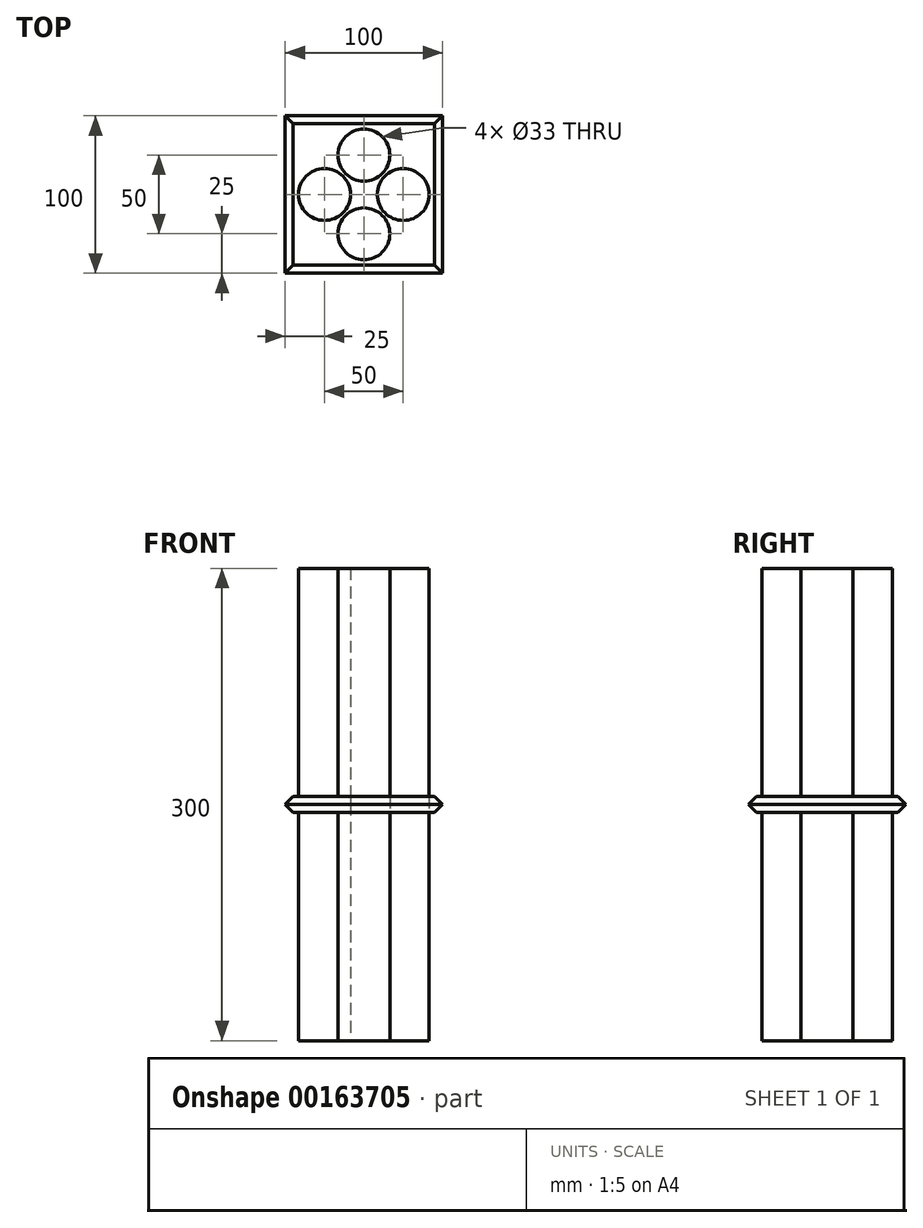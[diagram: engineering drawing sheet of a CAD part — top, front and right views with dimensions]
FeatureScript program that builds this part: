
annotation { "Feature Type Name" : "Feature", "Feature Type Description" : "" }
export const myFeature = defineFeature(function(context is Context, id is Id, definition is map)
    precondition{}
    {
        {
            var Q0;
            Q0=qCreatedBy(makeId("Top.planeOp"),FACE);
            var sketch = newSketch(context, id + "F0", { "sketchPlane" : qUnion([Q0])});
            skLineSegment(sketch, "E0.bottom", {"start": v(50, 50) * mm, "end": v(-50, 50) * mm});
            skLineSegment(sketch, "E0.top", {"start": v(50, -50) * mm, "end": v(-50, -50) * mm});
            skLineSegment(sketch, "E0.left", {"start": v(50, 50) * mm, "end": v(50, -50) * mm});
            skLineSegment(sketch, "E0.right", {"start": v(-50, 50) * mm, "end": v(-50, -50) * mm});
            skPoint(sketch, "E0.middle", {"position": v(0, 0) * mm});
            skCircle(sketch, "E1", {"center": v(25, 0) * mm, "radius": 16.5 * mm});
            skCircle(sketch, "E2", {"center": v(-25, 0) * mm, "radius": 16.5 * mm});
            skCircle(sketch, "E3", {"center": v(0, 25) * mm, "radius": 16.5 * mm});
            skCircle(sketch, "E4", {"center": v(0, -25) * mm, "radius": 16.5 * mm});
            skLineSegment(sketch, "E5", {"start": v(-25, 0) * mm, "end": v(-25, -33.27) * mm});
            skLineSegment(sketch, "E6", {"start": v(0, -25) * mm, "end": v(35.94, -25) * mm});
            skLineSegment(sketch, "E7", {"start": v(25, 0) * mm, "end": v(25, 37.48) * mm});
            skLineSegment(sketch, "E8", {"start": v(0, 25) * mm, "end": v(-38.74, 25) * mm});
            skSolve(sketch);
        }
        {
            var Q0;
            Q0=makeQuery(id+"F0.imprint","IMPRINT",FACE,{"disambiguationData":[TD([[makeQuery(id+"F0.imprint","IMPRINT",EDGE,{"derivedFrom":sQuery(id+"F0.wireOp",EDGE,"E3")}),1.0]])]});
            var Q1;
            Q1=makeQuery(id+"F0.imprint","IMPRINT",FACE,{"disambiguationData":[TD([[makeQuery(id+"F0.imprint","IMPRINT",EDGE,{"derivedFrom":sQuery(id+"F0.wireOp",EDGE,"E2")}),1.0]])]});
            var Q2;
            Q2=makeQuery(id+"F0.imprint","IMPRINT",FACE,{"disambiguationData":[TD([[makeQuery(id+"F0.imprint","IMPRINT",EDGE,{"derivedFrom":sQuery(id+"F0.wireOp",EDGE,"E1")}),1.0]])]});
            var Q3;
            Q3=makeQuery(id+"F0.imprint","IMPRINT",FACE,{"disambiguationData":[TD([[makeQuery(id+"F0.imprint","IMPRINT",EDGE,{"derivedFrom":sQuery(id+"F0.wireOp",EDGE,"E4")}),1.0]])]});
            extrude(context, id + "F1", {"entities" : qUnion([Q0, Q1, Q2, Q3]), "endBound" : BoundingType.SYMMETRIC, "depth" : 300 * mm});
        }
        {
            var Q0;
            Q0=makeQuery(id+"F0.imprint","IMPRINT",FACE,{"disambiguationData":[TD([[makeQuery(id+"F0.imprint","IMPRINT",EDGE,{"derivedFrom":sQuery(id+"F0.wireOp",EDGE,"E0.bottom")}),1.0]])]});
            extrude(context, id + "F2", {"entities" : qUnion([Q0]), "endBound" : BoundingType.SYMMETRIC, "depth" : 10 * mm});
        }
        {
            var Q0;
            Q0=makeQuery(id+"F2.opExtrude","CAP_EDGE",EDGE,{"disambiguationData":[OSD([sQuery(id+"F0.wireOp",EDGE,"E0.top")])],"isStart":false});
            var Q1;
            Q1=makeQuery(id+"F2.opExtrude","CAP_EDGE",EDGE,{"disambiguationData":[OSD([sQuery(id+"F0.wireOp",EDGE,"E0.left")])],"isStart":false});
            var Q2;
            Q2=makeQuery(id+"F2.opExtrude","CAP_EDGE",EDGE,{"disambiguationData":[OSD([sQuery(id+"F0.wireOp",EDGE,"E0.right")])],"isStart":false});
            var Q3;
            Q3=makeQuery(id+"F2.opExtrude","CAP_EDGE",EDGE,{"disambiguationData":[OSD([sQuery(id+"F0.wireOp",EDGE,"E0.bottom")])],"isStart":false});
            chamfer(context, id + "F3", {"entities" : qUnion([Q0, Q1, Q2, Q3]), "width" : 5 * mm, "tangentPropagation" : true});
        }
        {
            var Q0;
            Q0=makeQuery(id+"F2.opExtrude","CAP_EDGE",EDGE,{"disambiguationData":[OSD([sQuery(id+"F0.wireOp",EDGE,"E0.bottom")])],"isStart":true});
            var Q1;
            Q1=makeQuery(id+"F2.opExtrude","CAP_EDGE",EDGE,{"disambiguationData":[OSD([sQuery(id+"F0.wireOp",EDGE,"E0.left")])],"isStart":true});
            var Q2;
            Q2=makeQuery(id+"F2.opExtrude","CAP_EDGE",EDGE,{"disambiguationData":[OSD([sQuery(id+"F0.wireOp",EDGE,"E0.top")])],"isStart":true});
            var Q3;
            Q3=makeQuery(id+"F2.opExtrude","CAP_EDGE",EDGE,{"disambiguationData":[OSD([sQuery(id+"F0.wireOp",EDGE,"E0.right")])],"isStart":true});
            chamfer(context, id + "F4", {"entities" : qUnion([Q0, Q1, Q2, Q3]), "width" : 5 * mm, "tangentPropagation" : true});
        }
    });
